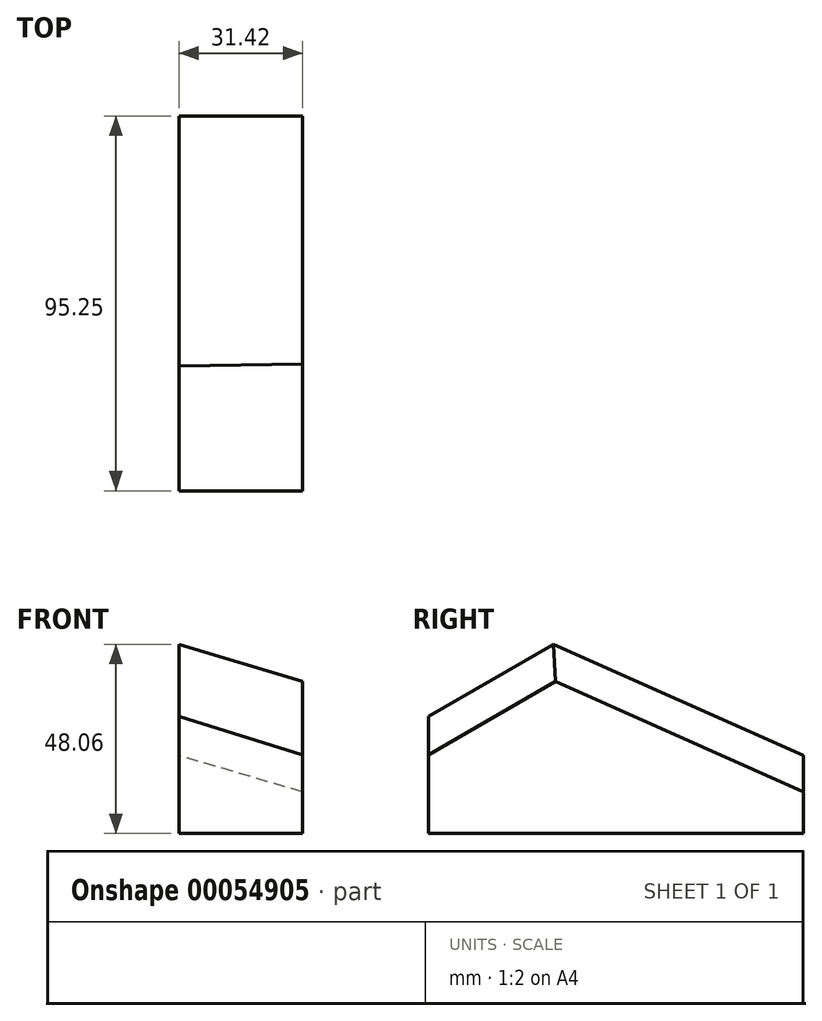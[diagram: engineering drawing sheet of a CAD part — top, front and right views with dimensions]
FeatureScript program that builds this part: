
annotation { "Feature Type Name" : "Feature", "Feature Type Description" : "" }
export const myFeature = defineFeature(function(context is Context, id is Id, definition is map)
    precondition{}
    {
        {
            var Q0;
            Q0=qCreatedBy(makeId("Front.planeOp"),FACE);
            var sketch = newSketch(context, id + "F0", { "sketchPlane" : qUnion([Q0])});
            skLineSegment(sketch, "E0.rect.bottom", {"start": v(-15.7, 25.4) * mm, "end": v(15.7, 25.4) * mm});
            skLineSegment(sketch, "E0.rect.top", {"start": v(-15.7, -25.4) * mm, "end": v(15.7, -25.4) * mm});
            skLineSegment(sketch, "E0.rect.left", {"start": v(-15.7, 25.4) * mm, "end": v(-15.7, -25.4) * mm});
            skLineSegment(sketch, "E0.rect.right", {"start": v(15.7, 25.4) * mm, "end": v(15.7, -25.4) * mm});
            skPoint(sketch, "E0.rect.middle", {"position": v(0, 0) * mm});
            skSolve(sketch);
        }
        {
            var Q0;
            Q0=makeQuery(id+"F0.imprint","IMPRINT",FACE,{"disambiguationData":[TD([[makeQuery(id+"F0.imprint","IMPRINT",EDGE,{"derivedFrom":sQuery(id+"F0.wireOp",EDGE,"E0.rect.bottom")}),-1.0]])]});
            extrude(context, id + "F1", {"entities" : qUnion([Q0]), "depth" : 95.25 * mm, "symmetric" : true});
        }
        {
            var Q0;
            Q0=makeQuery(id+"F1.opExtrude","CAP_EDGE",EDGE,{"disambiguationData":[OSD([sQuery(id+"F0.wireOp",EDGE,"E0.rect.bottom")])],"isStart":true});
            chamfer(context, id + "F2", {"entities" : qUnion([Q0]), "chamferType" : ChamferType.OFFSET_ANGLE, "width" : 30.48 * mm, "oppositeDirection" : false, "angle" : 66 * degree});
        }
        {
            var Q0;
            {var subQ0=sQuery(id+"F0.wireOp",EDGE,"E0.rect.bottom");Q0=makeQuery(id+"F2.opChamfer","BLEND_EDGE",EDGE,{"blendedFrom":[makeQuery(id+"F1.opExtrude","CAP_EDGE",EDGE,{"disambiguationData":[OSD([subQ0])],"isStart":true}),makeQuery(id+"F1.opExtrude","CAP_FACE",FACE,{"disambiguationData":[OSD([subQ0,sQuery(id+"F0.wireOp",EDGE,"E0.rect.top"),sQuery(id+"F0.wireOp",EDGE,"E0.rect.left"),sQuery(id+"F0.wireOp",EDGE,"E0.rect.right")])],"isStart":false})],"blendedInto":[makeQuery(id+"F1.opExtrude","CAP_FACE",FACE,{"disambiguationData":[OSD([subQ0,sQuery(id+"F0.wireOp",EDGE,"E0.rect.top"),sQuery(id+"F0.wireOp",EDGE,"E0.rect.left"),sQuery(id+"F0.wireOp",EDGE,"E0.rect.right")])],"isStart":false})]});}
            var Q1;
            Q1=makeQuery(id+"F1.opExtrude","CAP_EDGE",EDGE,{"disambiguationData":[OSD([sQuery(id+"F0.wireOp",EDGE,"E0.rect.bottom")])],"isStart":false});
            chamfer(context, id + "F3", {"entities" : qUnion([Q0, Q1]), "chamferType" : ChamferType.OFFSET_ANGLE, "width" : 35.56 * mm, "oppositeDirection" : false, "angle" : 30 * degree, "tangentPropagation" : true});
        }
        {
            var Q0;
            Q0=makeQuery(id+"F3.opChamfer","BLEND_EDGE",EDGE,{"blendedFrom":[makeQuery(id+"F1.opExtrude","CAP_EDGE",EDGE,{"disambiguationData":[OSD([sQuery(id+"F0.wireOp",EDGE,"E0.rect.bottom")])],"isStart":false}),makeQuery(id+"F1.opExtrude","SWEPT_FACE",FACE,{"disambiguationData":[OSD([sQuery(id+"F0.wireOp",EDGE,"E0.rect.right")])]})],"blendedInto":[makeQuery(id+"F1.opExtrude","SWEPT_FACE",FACE,{"disambiguationData":[OSD([sQuery(id+"F0.wireOp",EDGE,"E0.rect.right")])]})]});
            var Q1;
            Q1=makeQuery(id+"F2.opChamfer","BLEND_EDGE",EDGE,{"blendedFrom":[makeQuery(id+"F1.opExtrude","CAP_EDGE",EDGE,{"disambiguationData":[OSD([sQuery(id+"F0.wireOp",EDGE,"E0.rect.bottom")])],"isStart":true}),makeQuery(id+"F1.opExtrude","SWEPT_FACE",FACE,{"disambiguationData":[OSD([sQuery(id+"F0.wireOp",EDGE,"E0.rect.right")])]})],"blendedInto":[makeQuery(id+"F1.opExtrude","SWEPT_FACE",FACE,{"disambiguationData":[OSD([sQuery(id+"F0.wireOp",EDGE,"E0.rect.right")])]})]});
            chamfer(context, id + "F4", {"entities" : qUnion([Q0, Q1]), "chamferType" : ChamferType.OFFSET_ANGLE, "width" : 8.9 * mm, "oppositeDirection" : false, "angle" : 75 * degree, "tangentPropagation" : true});
        }
    });
